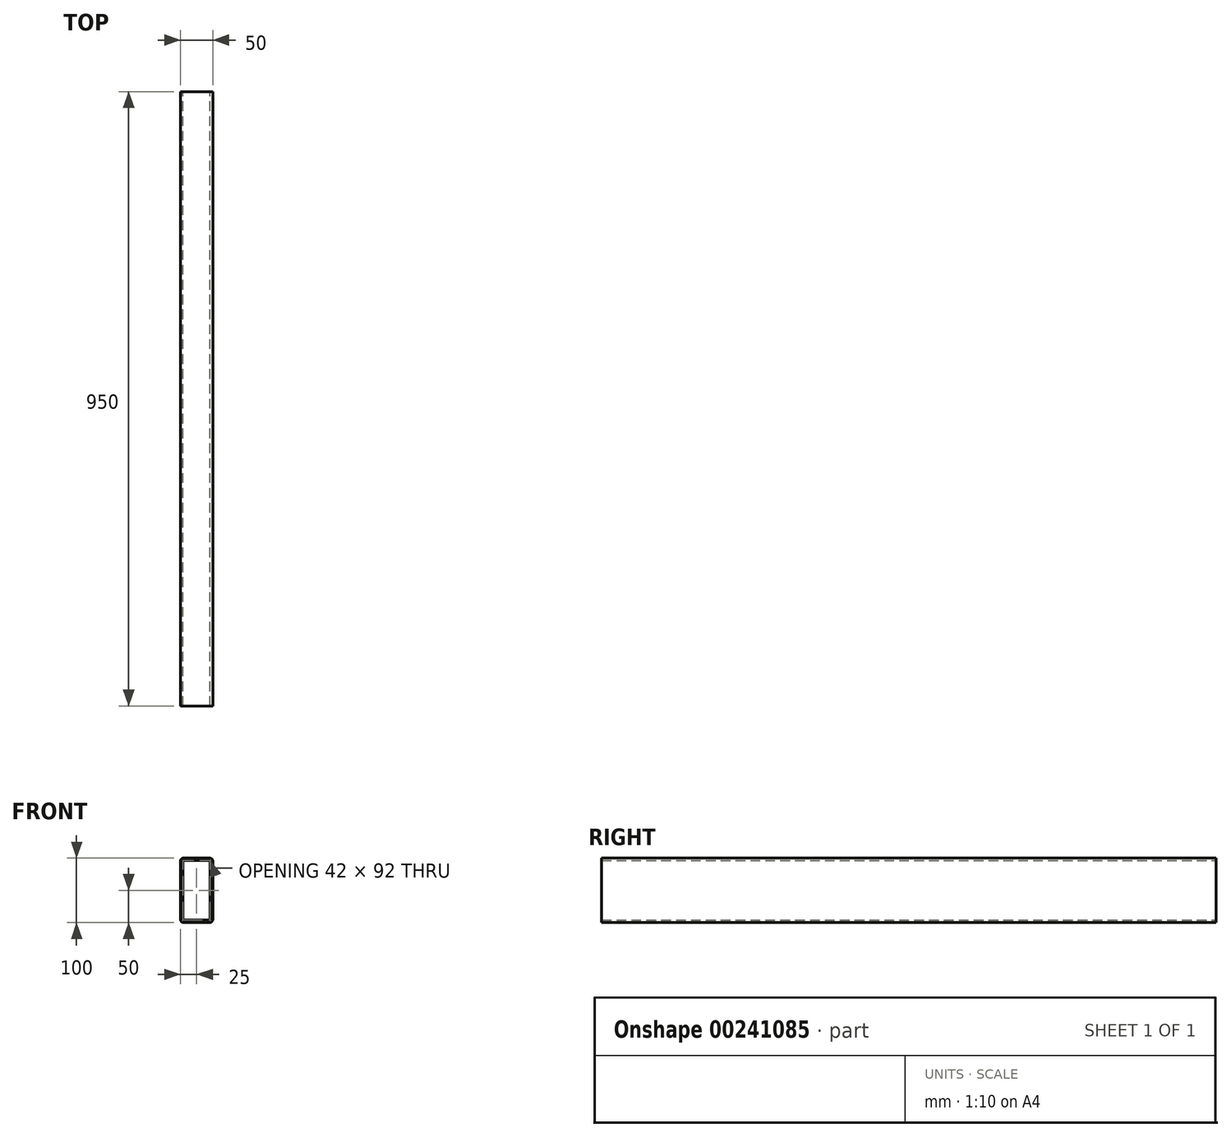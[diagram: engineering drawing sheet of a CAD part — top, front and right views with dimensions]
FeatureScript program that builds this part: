
annotation { "Feature Type Name" : "Feature", "Feature Type Description" : "" }
export const myFeature = defineFeature(function(context is Context, id is Id, definition is map)
    precondition{}
    {
        {
            var Q0;
            Q0=qCreatedBy(makeId("Top.planeOp"),FACE);
            var sketch = newSketch(context, id + "F0", { "sketchPlane" : qUnion([Q0])});
            skLineSegment(sketch, "E0.bottom", {"start": v(0, 0) * mm, "end": v(-50, 0) * mm});
            skLineSegment(sketch, "E0.top", {"start": v(0, 950) * mm, "end": v(-50, 950) * mm});
            skLineSegment(sketch, "E0.left", {"start": v(0, 0) * mm, "end": v(0, 950) * mm});
            skLineSegment(sketch, "E0.right", {"start": v(-50, 0) * mm, "end": v(-50, 950) * mm});
            skSolve(sketch);
        }
        {
            var Q0;
            Q0=makeQuery(id+"F0.imprint","IMPRINT",FACE,{"disambiguationData":[TD([[makeQuery(id+"F0.imprint","IMPRINT",EDGE,{"derivedFrom":sQuery(id+"F0.wireOp",EDGE,"E0.bottom")}),-1.0]])]});
            extrude(context, id + "F1", {"entities" : qUnion([Q0]), "depth" : 100 * mm});
        }
        {
            var Q0;
            Q0=makeQuery(id+"F1.opExtrude","CAP_EDGE",EDGE,{"disambiguationData":[OSD([sQuery(id+"F0.wireOp",EDGE,"E0.left")])],"isStart":false});
            var Q1;
            Q1=makeQuery(id+"F1.opExtrude","CAP_EDGE",EDGE,{"disambiguationData":[OSD([sQuery(id+"F0.wireOp",EDGE,"E0.right")])],"isStart":false});
            var Q2;
            Q2=makeQuery(id+"F1.opExtrude","CAP_EDGE",EDGE,{"disambiguationData":[OSD([sQuery(id+"F0.wireOp",EDGE,"E0.left")])],"isStart":true});
            var Q3;
            Q3=makeQuery(id+"F1.opExtrude","CAP_EDGE",EDGE,{"disambiguationData":[OSD([sQuery(id+"F0.wireOp",EDGE,"E0.right")])],"isStart":true});
            fillet(context, id + "F2", {"entities" : qUnion([Q0, Q1, Q2, Q3]), "radius" : 5 * mm, "tangentPropagation" : true, "allowEdgeOverflow" : false});
        }
        {
            var Q0;
            Q0=makeQuery(id+"F1.opExtrude","SWEPT_FACE",FACE,{"disambiguationData":[OSD([sQuery(id+"F0.wireOp",EDGE,"E0.bottom")])]});
            var Q1;
            Q1=makeQuery(id+"F1.opExtrude","SWEPT_FACE",FACE,{"disambiguationData":[OSD([sQuery(id+"F0.wireOp",EDGE,"E0.top")])]});
            shell(context, id + "F3", {"entities" : qUnion([Q0, Q1]), "thickness" : 4 * mm});
        }
    });
